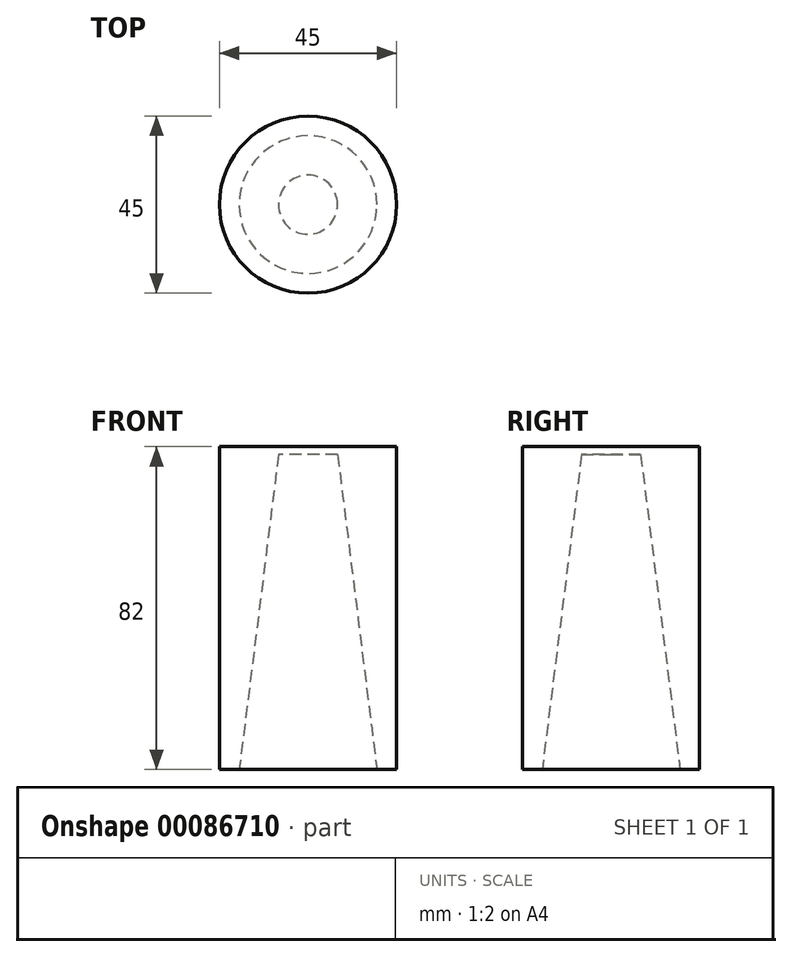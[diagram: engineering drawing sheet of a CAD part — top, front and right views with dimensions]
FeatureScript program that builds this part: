
annotation { "Feature Type Name" : "Feature", "Feature Type Description" : "" }
export const myFeature = defineFeature(function(context is Context, id is Id, definition is map)
    precondition{}
    {
        {
            var Q0;
            Q0=qCreatedBy(makeId("Top.planeOp"),FACE);
            var sketch = newSketch(context, id + "F0", { "sketchPlane" : qUnion([Q0])});
            skCircle(sketch, "E0", {"center": v(0, 0) * mm, "radius": 17.5 * mm});
            skSolve(sketch);
        }
        {
            var Q0;
            Q0=qCreatedBy(makeId("Top.planeOp"),FACE);
            cPlane(context, id + "F1", {"entities" : qUnion([Q0]), "cplaneType" : CPlaneType.OFFSET, "offset" : 80 * mm, "width" : 150 * mm, "height" : 150 * mm});
        }
        {
            var Q0;
            Q0=qCreatedBy(id+"F1.planeOp",FACE);
            var sketch = newSketch(context, id + "F2", { "sketchPlane" : qUnion([Q0])});
            skCircle(sketch, "E1", {"center": v(0, 0) * mm, "radius": 7.5 * mm});
            skSolve(sketch);
        }
        {
            var Q0;
            Q0=qCreatedBy(makeId("Top.planeOp"),FACE);
            var sketch = newSketch(context, id + "F3", { "sketchPlane" : qUnion([Q0])});
            skCircle(sketch, "E2", {"center": v(0, 0) * mm, "radius": 22.5 * mm});
            skSolve(sketch);
        }
        {
            var Q0;
            Q0=makeQuery(id+"F3.imprint","IMPRINT",FACE,{"disambiguationData":[TD([[makeQuery(id+"F3.imprint","IMPRINT",EDGE,{"derivedFrom":sQuery(id+"F3.wireOp",EDGE,"E2")}),1.0]])]});
            extrude(context, id + "F4", {"entities" : qUnion([Q0]), "depth" : 80 * mm});
        }
        {
            var Q1;
            Q1=makeQuery(id+"F2.imprint","IMPRINT",FACE,{"disambiguationData":[TD([[makeQuery(id+"F2.imprint","IMPRINT",EDGE,{"derivedFrom":sQuery(id+"F2.wireOp",EDGE,"E1")}),1.0]])]});
            var Q2;
            Q2=makeQuery(id+"F0.imprint","IMPRINT",FACE,{"disambiguationData":[TD([[makeQuery(id+"F0.imprint","IMPRINT",EDGE,{"derivedFrom":sQuery(id+"F0.wireOp",EDGE,"E0")}),1.0]])]});
            loft(context, id + "F5", {"operationType" : NewBodyOperationType.REMOVE, "sheetProfilesArray" : [{ "sheetProfileEntities" : qUnion([Q1]) }, { "sheetProfileEntities" : qUnion([Q2]) }]});
        }
        {
            var Q0;
            Q0=qSketchRegion(id+"F2",true);
            var Q1;
            Q1=makeQuery(id+"F4.opExtrude","CAP_FACE",FACE,{"disambiguationData":[OSD([sQuery(id+"F3.wireOp",EDGE,"E2")])],"isStart":false});
            extrude(context, id + "F6", {"entities" : qUnion([Q0, Q1]), "operationType" : NewBodyOperationType.ADD, "depth" : 2 * mm});
        }
    });
